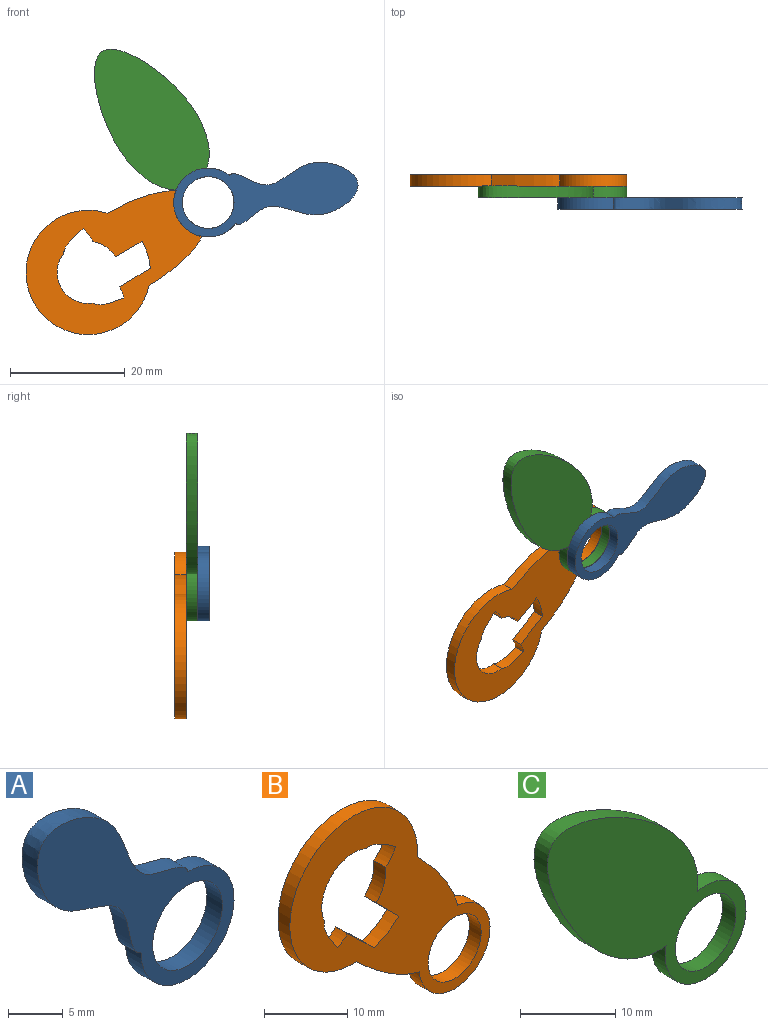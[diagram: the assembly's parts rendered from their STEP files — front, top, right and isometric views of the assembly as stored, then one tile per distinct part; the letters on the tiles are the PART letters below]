
ASSEMBLY  parts=3 mates=2
PART A: 5 faces, bbox 25.8x2x25.8 mm
  f0: extruded ~19.35x19.33mm, area 100.8mm2, adj f1,f3,f4
  f1: cylinder r=6mm len=12mm, axis (0,1,0), area 56.5mm2, adj f0,f3,f4
  f2: cylinder r=4.5mm len=9mm, axis (0,1,0), area 56.5mm2, adj f3,f4
  f3: plane 25.77x25.76mm, normal (0,-1,0), area 185mm2, adj f0,f1,f2
  f4: plane 25.77x25.76mm, normal (0,1,0), area 185mm2, adj f0,f1,f2
PART B: 16 faces, bbox 33.9x2x33.9 mm
  f0: cylinder r=10.83mm len=21.66mm, axis (0,1,0), area 104.2mm2, adj f1,f11,f14,f15
  f1: extruded ~10.58x6.79mm, area 25.4mm2, adj f0,f2,f14,f15
  f2: cylinder r=6mm len=11.98mm, axis (0,1,0), area 54.5mm2, adj f1,f11,f14,f15
  f3: cylinder r=10.83mm len=4.16mm, axis (0,1,0), area 9.9mm2, adj f4,f12,f14,f15
  f4: plane 4.52x4.34mm, normal (0.69,0,0.72), area 12.5mm2, adj f3,f5,f14,f15
  f5: cylinder r=5.42mm len=2mm, axis (0,1,0), area 4.2mm2, adj f4,f6,f14,f15
  f6: extruded ~4.95x2.27mm, area 11.1mm2, adj f5,f7,f14,f15
  f7: cylinder r=5.42mm len=7.59mm, axis (0,1,0), area 26mm2, adj f6,f8,f14,f15
  f8: extruded ~4.95x2.27mm, area 11.1mm2, adj f7,f9,f14,f15
  f9: cylinder r=5.42mm len=2.16mm, axis (0,1,0), area 5.6mm2, adj f8,f10,f14,f15
  f10: cylinder r=5.42mm len=4.45mm, axis (0,1,0), area 9.8mm2, adj f9,f12,f14,f15
  f11: extruded ~10.58x6.79mm, area 25.4mm2, adj f0,f2,f14,f15
  f12: plane 3.85x3.81mm, normal (-0.71,0,-0.7), area 10.8mm2, adj f3,f10,f14,f15
  f13: cylinder r=4.5mm len=9mm, axis (0,1,0), area 56.5mm2, adj f14,f15
  f14: plane 33.92x33.92mm, normal (0,-1,0), area 401.8mm2, adj f0,f1,f2,f3,f4,f5,f6,f7
  f15: plane 33.92x33.92mm, normal (0,1,0), area 401.8mm2, adj f0,f1,f2,f3,f4,f5,f6,f7
PART C: 5 faces, bbox 30.2x2x30.2 mm
  f0: extruded ~22.34x22.34mm, area 123.3mm2, adj f1,f3,f4
  f1: cylinder r=6mm len=12mm, axis (0,1,0), area 61.6mm2, adj f0,f3,f4
  f2: cylinder r=4.5mm len=9mm, axis (0,1,0), area 56.5mm2, adj f3,f4
  f3: plane 30.23x30.23mm, normal (0,-1,0), area 357.3mm2, adj f0,f1,f2
  f4: plane 30.23x30.23mm, normal (0,1,0), area 357.3mm2, adj f0,f1,f2
PLACE A rot(axis=(0,1,0),127.8deg) t=(-0.1,4.64,0.95)mm
PLACE B rot(axis=(0,-1,0),75.2deg) t=(-0.1,8.64,0.95)mm
PLACE C rot(axis=(0,1,0),9.8deg) t=(-0.1,6.64,0.95)mm
MATE revolute A.f2 <-> C.f2  axis (0,1,0) through (-0.1,4.64,0.95)mm
MATE revolute C.f2 <-> B.f2  axis (0,1,0) through (-0.1,6.64,0.95)mm
